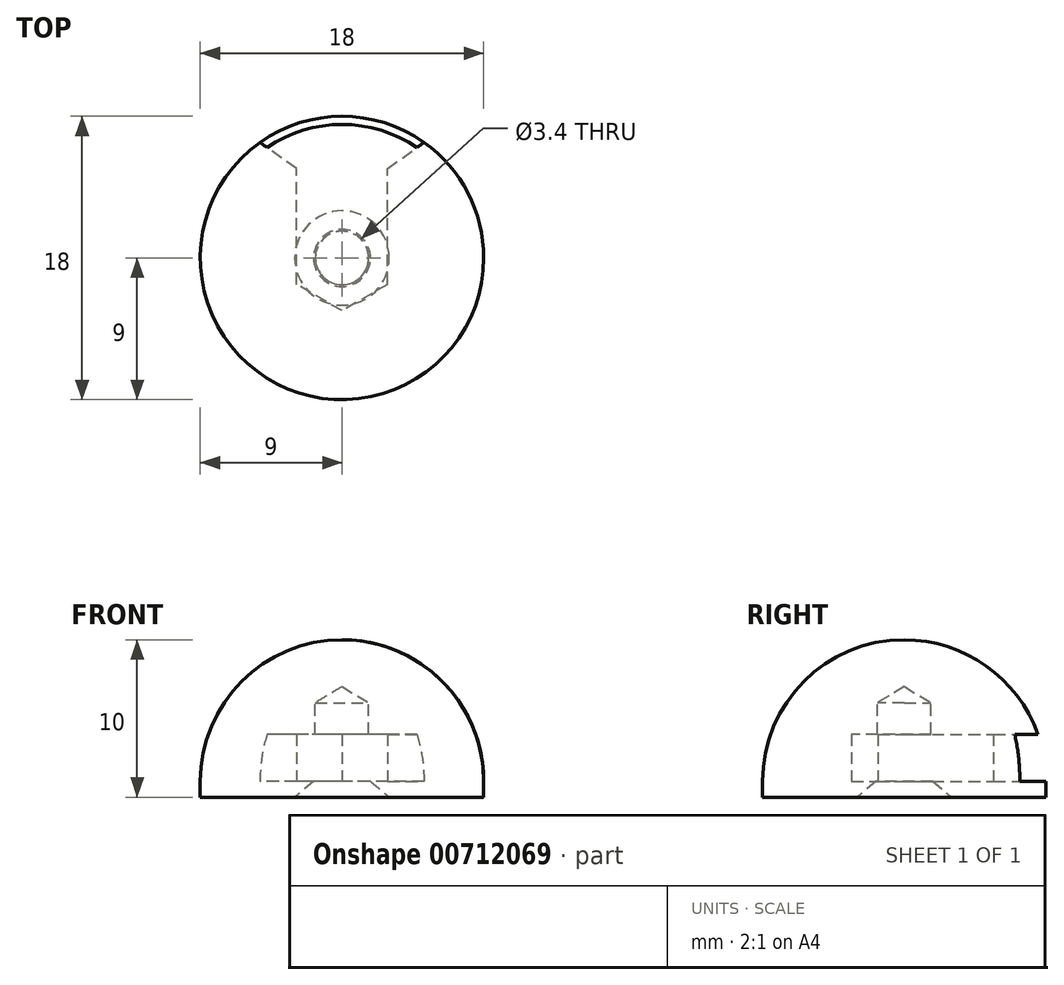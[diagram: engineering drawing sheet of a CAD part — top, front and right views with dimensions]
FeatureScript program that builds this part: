
annotation { "Feature Type Name" : "Feature", "Feature Type Description" : "" }
export const myFeature = defineFeature(function(context is Context, id is Id, definition is map)
    precondition{}
    {
        {
            var Q0;
            Q0=qCreatedBy(makeId("Top.planeOp"),FACE);
            var sketch = newSketch(context, id + "F0", { "sketchPlane" : qUnion([Q0])});
            skCircle(sketch, "E0", {"center": v(0, 0) * mm, "radius": 9 * mm});
            skSolve(sketch);
        }
        {
            var Q0;
            Q0=makeQuery(id+"F0.imprint","IMPRINT",FACE,{"disambiguationData":[TD([[makeQuery(id+"F0.imprint","IMPRINT",EDGE,{"derivedFrom":sQuery(id+"F0.wireOp",EDGE,"E0")}),1.0]])]});
            extrude(context, id + "F1", {"entities" : qUnion([Q0]), "depth" : 1 * mm, "offsetDistance" : 25 * mm});
        }
        {
            var Q0;
            Q0=makeQuery(id+"F1.opExtrude","CAP_FACE",FACE,{"disambiguationData":[OSD([sQuery(id+"F0.wireOp",EDGE,"E0")])],"isStart":false});
            var sketch = newSketch(context, id + "F2", { "sketchPlane" : qUnion([Q0])});
            skLineSegment(sketch, "E1.1", {"start": v(2.9, 1.67) * mm, "end": v(2.9, -1.67) * mm});
            skLineSegment(sketch, "E1.2", {"start": v(2.9, -1.67) * mm, "end": v(0, -3.35) * mm});
            skLineSegment(sketch, "E1.3", {"start": v(0, -3.35) * mm, "end": v(-2.9, -1.67) * mm});
            skLineSegment(sketch, "E1.4", {"start": v(-2.9, -1.67) * mm, "end": v(-2.9, 1.67) * mm});
            skLineSegment(sketch, "E2", {"start": v(-2.9, 1.67) * mm, "end": v(-2.9, 5.67) * mm});
            skLineSegment(sketch, "E3", {"start": v(2.9, 1.67) * mm, "end": v(2.9, 5.67) * mm});
            skLineSegment(sketch, "E4", {"start": v(2.9, 5.67) * mm, "end": v(5.2, 7.34) * mm});
            skLineSegment(sketch, "E5.MirrorCS", {"start": v(-2.9, 5.67) * mm, "end": v(-5.2, 7.34) * mm});
            skSolve(sketch);
        }
        {
            var Q0;
            Q0 = qSketchRegion(id + "F2", true);
            var Q1;
            Q1=makeQuery(id+"F2.imprint","IMPRINT",FACE,{"disambiguationData":[TD([[makeQuery(id+"F2.imprint","IMPRINT",EDGE,{"derivedFrom":sQuery(id+"F2.wireOp",EDGE,"E1.1")}),1.0]])]});
            extrude(context, id + "F3", {"entities" : qUnion([Q0, Q1]), "operationType" : NewBodyOperationType.ADD, "depth" : 3 * mm, "offsetDistance" : 25 * mm});
        }
        {
            var Q0;
            Q0=makeQuery(id+"F3.opExtrude","CAP_FACE",FACE,{"disambiguationData":[OSD([sQuery(id+"F0.wireOp",EDGE,"E0"),sQuery(id+"F2.wireOp",EDGE,"E1.1"),sQuery(id+"F2.wireOp",EDGE,"E1.2"),sQuery(id+"F2.wireOp",EDGE,"E1.3"),sQuery(id+"F2.wireOp",EDGE,"E1.4"),sQuery(id+"F2.wireOp",EDGE,"E2"),sQuery(id+"F2.wireOp",EDGE,"E3"),sQuery(id+"F2.wireOp",EDGE,"E4"),sQuery(id+"F2.wireOp",EDGE,"E5.MirrorCS")])],"isStart":false});
            var sketch = newSketch(context, id + "F4", { "sketchPlane" : qUnion([Q0])});
            skCircle(sketch, "E6", {"center": v(0, 0) * mm, "radius": 9 * mm});
            skSolve(sketch);
        }
        {
            var Q0;
            Q0 = qSketchRegion(id + "F4", true);
            extrude(context, id + "F5", {"entities" : qUnion([Q0]), "operationType" : NewBodyOperationType.ADD, "depth" : 6 * mm, "offsetDistance" : 25 * mm});
        }
        {
            var Q0;
            Q0=makeQuery(id+"F5.opExtrude","CAP_EDGE",EDGE,{"disambiguationData":[OSD([sQuery(id+"F4.wireOp",EDGE,"E6")])],"isStart":false});
            fillet(context, id + "F6", {"entities" : qUnion([Q0]), "radius" : 9 * mm, "tangentPropagation" : true, "allowEdgeOverflow" : false});
        }
        {
            var Q0;
            Q0=sQuery(id+"F0.wireOp",VERTEX,"E0.center");
            var Q1;
            Q1=makeQuery(id+"F1.opExtrude","SWEPT_BODY",BODY,{"disambiguationData":[OSD([sQuery(id+"F0.wireOp",EDGE,"E0")])]});
            hole(context, id + "F7", {"style" : HoleStyle.C_SINK, "endStyle" : HoleEndStyle.BLIND, "oppositeDirection" : true, "holeDiameter" : 3.4 * mm, "cSinkDiameter" : 6 * mm, "cSinkAngle" : 100 * degree, "majorDiameter" : 5 * mm, "holeDepth" : 6 * mm, "isTappedThrough" : true, "tappedDepth" : 12 * mm, "tapClearance" : 3, "locations" : qUnion([Q0]), "scope" : qUnion([Q1]), "startStyle" : HoleStartStyle.PART});
        }
    });
